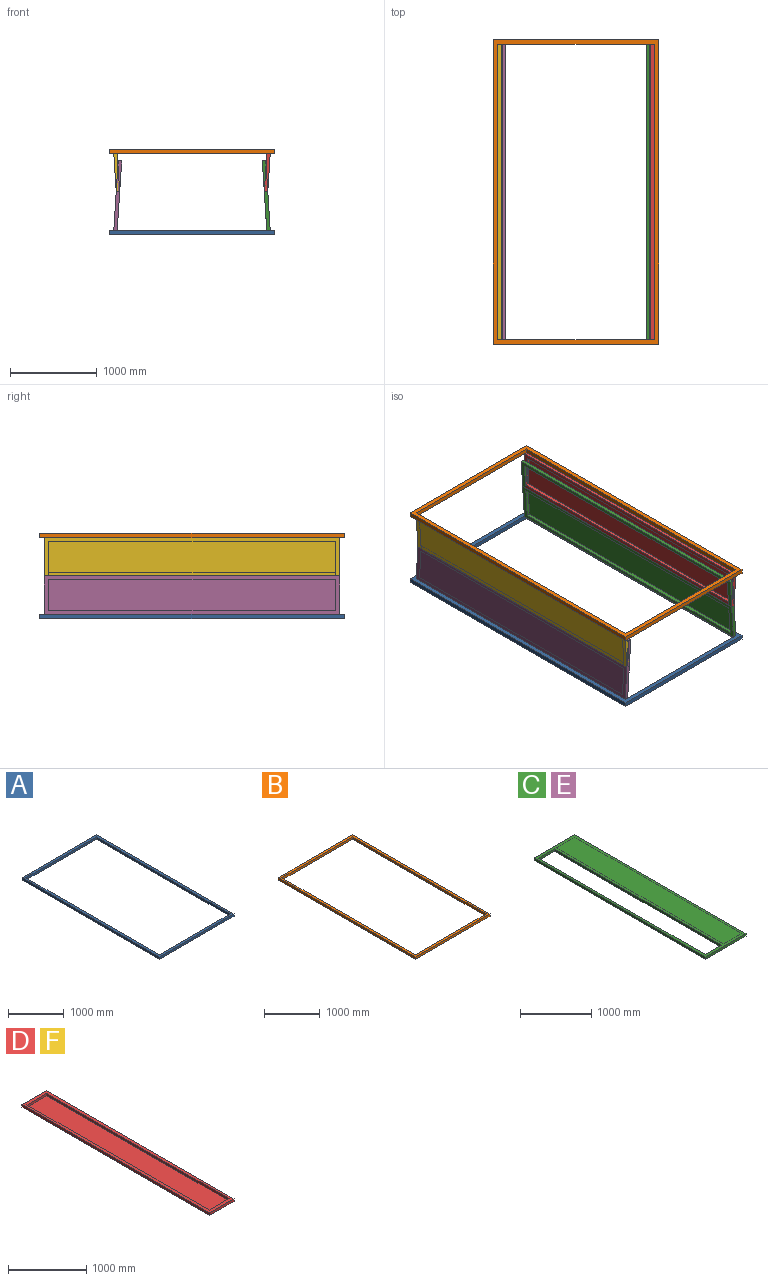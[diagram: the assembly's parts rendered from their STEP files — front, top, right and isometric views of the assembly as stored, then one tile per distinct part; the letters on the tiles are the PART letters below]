
ASSEMBLY  parts=6 mates=7
PART A: 10 faces, bbox 1900x3500x50 mm
  f0: plane 1800x50mm, normal (0,-1,0), area 90000mm2, adj f1,f7,f8,f9
  f1: plane 3400x50mm, normal (-1,0,0), area 170000mm2, adj f0,f2,f8,f9
  f2: plane 1800x50mm, normal (0,1,0), area 90000mm2, adj f1,f7,f8,f9
  f3: plane 3500x50mm, normal (1,0,0), area 175000mm2, adj f4,f6,f8,f9
  f4: plane 1900x50mm, normal (0,1,0), area 95000mm2, adj f3,f5,f8,f9
  f5: plane 3500x50mm, normal (-1,0,0), area 175000mm2, adj f4,f6,f8,f9
  f6: plane 1900x50mm, normal (0,-1,0), area 95000mm2, adj f3,f5,f8,f9
  f7: plane 3400x50mm, normal (1,0,0), area 170000mm2, adj f0,f2,f8,f9
  f8: plane 3500x1900mm, normal (0,0,1), area 530000mm2, adj f0,f1,f2,f3,f4,f5,f6,f7
  f9: plane 3500x1900mm, normal (0,0,-1), area 530000mm2, adj f0,f1,f2,f3,f4,f5,f6,f7
PART B: 10 faces, bbox 1900x3500x50 mm
  f0: plane 1800x50mm, normal (0,-1,0), area 90000mm2, adj f1,f7,f8,f9
  f1: plane 3400x50mm, normal (-1,0,0), area 170000mm2, adj f0,f2,f8,f9
  f2: plane 1800x50mm, normal (0,1,0), area 90000mm2, adj f1,f7,f8,f9
  f3: plane 3500x50mm, normal (1,0,0), area 175000mm2, adj f4,f6,f8,f9
  f4: plane 1900x50mm, normal (0,1,0), area 95000mm2, adj f3,f5,f8,f9
  f5: plane 3500x50mm, normal (-1,0,0), area 175000mm2, adj f4,f6,f8,f9
  f6: plane 1900x50mm, normal (0,-1,0), area 95000mm2, adj f3,f5,f8,f9
  f7: plane 3400x50mm, normal (1,0,0), area 170000mm2, adj f0,f2,f8,f9
  f8: plane 3500x1900mm, normal (0,0,1), area 530000mm2, adj f0,f1,f2,f3,f4,f5,f6,f7
  f9: plane 3500x1900mm, normal (0,0,-1), area 530000mm2, adj f0,f1,f2,f3,f4,f5,f6,f7
PART C: 15 faces, bbox 800x3400x40 mm
  f0: plane 3400x800mm, normal (0,0,-1), area 476000mm2, adj f2,f3,f4,f5,f6,f7,f8,f9
  f1: plane 3400x800mm, normal (0,0,1), area 1664000mm2, adj f2,f3,f4,f5,f10,f11,f12,f13
  f2: plane 3400x40mm, normal (1,0,0), area 136000mm2, adj f0,f1,f4,f5
  f3: plane 3400x40mm, normal (-1,0,0), area 136000mm2, adj f0,f1,f4,f5
  f4: plane 800x40mm, normal (0,-1,0), area 32000mm2, adj f0,f1,f2,f3
  f5: plane 800x40mm, normal (0,1,0), area 32000mm2, adj f0,f1,f2,f3
  f6: plane 3300x37mm, normal (-1,0,0), area 122100mm2, adj f0,f8,f9,f14
  f7: plane 3300x37mm, normal (1,0,0), area 122100mm2, adj f0,f8,f9,f14
  f8: plane 360x37mm, normal (0,-1,0), area 13320mm2, adj f0,f6,f7,f14
  f9: plane 360x37mm, normal (0,1,0), area 13320mm2, adj f0,f6,f7,f14
  f10: plane 3300x40mm, normal (1,0,0), area 132000mm2, adj f0,f1,f12,f13
  f11: plane 3300x40mm, normal (-1,0,0), area 132000mm2, adj f0,f1,f12,f13
  f12: plane 320x40mm, normal (0,-1,0), area 12800mm2, adj f0,f1,f10,f11
  f13: plane 320x40mm, normal (0,1,0), area 12800mm2, adj f0,f1,f10,f11
  f14: plane 3300x360mm, normal (0,0,-1), area 1188000mm2, adj f6,f7,f8,f9
PART D: 11 faces, bbox 440x3400x40 mm
  f0: plane 3300x37mm, normal (-1,0,0), area 122100mm2, adj f1,f2,f4,f10
  f1: plane 360x37mm, normal (0,-1,0), area 13320mm2, adj f0,f4,f9,f10
  f2: plane 360x37mm, normal (0,1,0), area 13320mm2, adj f0,f4,f9,f10
  f3: plane 3400x440mm, normal (0,0,-1), area 1496000mm2, adj f5,f6,f7,f8
  f4: plane 3400x440mm, normal (0,0,1), area 308000mm2, adj f0,f1,f2,f5,f6,f7,f8,f9
  f5: plane 3400x40mm, normal (1,0,0), area 136000mm2, adj f3,f4,f7,f8
  f6: plane 3400x40mm, normal (-1,0,0), area 136000mm2, adj f3,f4,f7,f8
  f7: plane 440x40mm, normal (0,-1,0), area 17600mm2, adj f3,f4,f5,f6
  f8: plane 440x40mm, normal (0,1,0), area 17600mm2, adj f3,f4,f5,f6
  f9: plane 3300x37mm, normal (1,0,0), area 122100mm2, adj f1,f2,f4,f10
  f10: plane 3300x360mm, normal (0,0,1), area 1188000mm2, adj f0,f1,f2,f9
PART E: same geometry as C
PART F: same geometry as D
PLACE A t=(523.49,19.47,-33.93)mm fixed
PLACE B t=(523.49,19.47,-105.74)mm
PLACE C rot(axis=(0,1,0),86.3deg) t=(1316,19.47,911.02)mm
PLACE D rot(axis=(0,-1,0),86.3deg) t=(1415.8,19.47,-7.09)mm
PLACE E rot(axis=(-0.68,0,0.73),180deg) t=(-269.02,19.47,911.02)mm
PLACE F rot(axis=(0,1,0),86.3deg) t=(-455.84,19.47,1350.12)mm
MATE revolute C.f4 <-> A.f2  axis (0,-1,0) through (1423.49,-1680.53,16.07)mm
MATE cylindrical F.f7 <-> E.f12  axis (0,-1,0) through (-348.35,-1680.53,455.16)mm
MATE slider B.f9 <-> A.f8  axis (0,0,-1) through (1473.49,-1730.53,894.26)mm
MATE revolute F.f7 <-> B.f2  axis (0,-1,0) through (-376.51,-1680.53,894.26)mm
MATE revolute E.f5 <-> A.f2  axis (0,-1,0) through (-376.51,-1680.53,16.07)mm
MATE revolute B.f2 <-> D.f7  axis (0,1,0) through (1423.49,-1680.53,894.26)mm
MATE cylindrical D.f7 <-> C.f13  axis (0,-1,0) through (1395.34,-1680.53,455.16)mm
